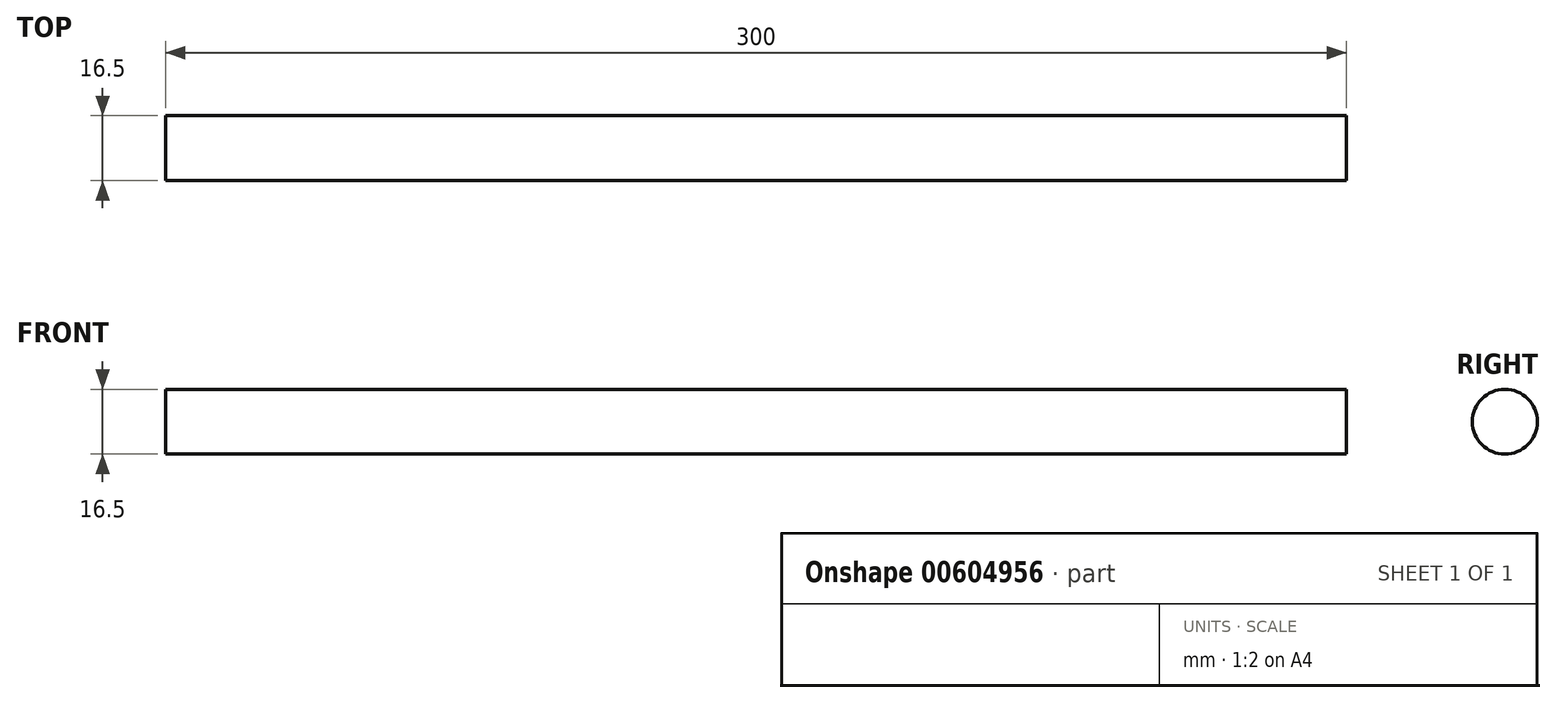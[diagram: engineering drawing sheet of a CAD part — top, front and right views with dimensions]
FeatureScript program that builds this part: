
annotation { "Feature Type Name" : "Feature", "Feature Type Description" : "" }
export const myFeature = defineFeature(function(context is Context, id is Id, definition is map)
    precondition{}
    {
        {
            var Q0;
            Q0=qCreatedBy(makeId("Right.planeOp"),FACE);
            var sketch = newSketch(context, id + "F0", { "sketchPlane" : qUnion([Q0])});
            skCircle(sketch, "E0", {"center": v(0, 0) * mm, "radius": 8.25 * mm});
            skSolve(sketch);
        }
        {
            var Q0;
            Q0=makeQuery(id+"F0.imprint","IMPRINT",FACE,{"disambiguationData":[TD([[makeQuery(id+"F0.imprint","IMPRINT",EDGE,{"derivedFrom":sQuery(id+"F0.wireOp",EDGE,"E0")}),1.0]])]});
            extrude(context, id + "F1", {"entities" : qUnion([Q0]), "depth" : 300 * mm, "offsetDistance" : 25 * mm, "symmetric" : true});
        }
    });
